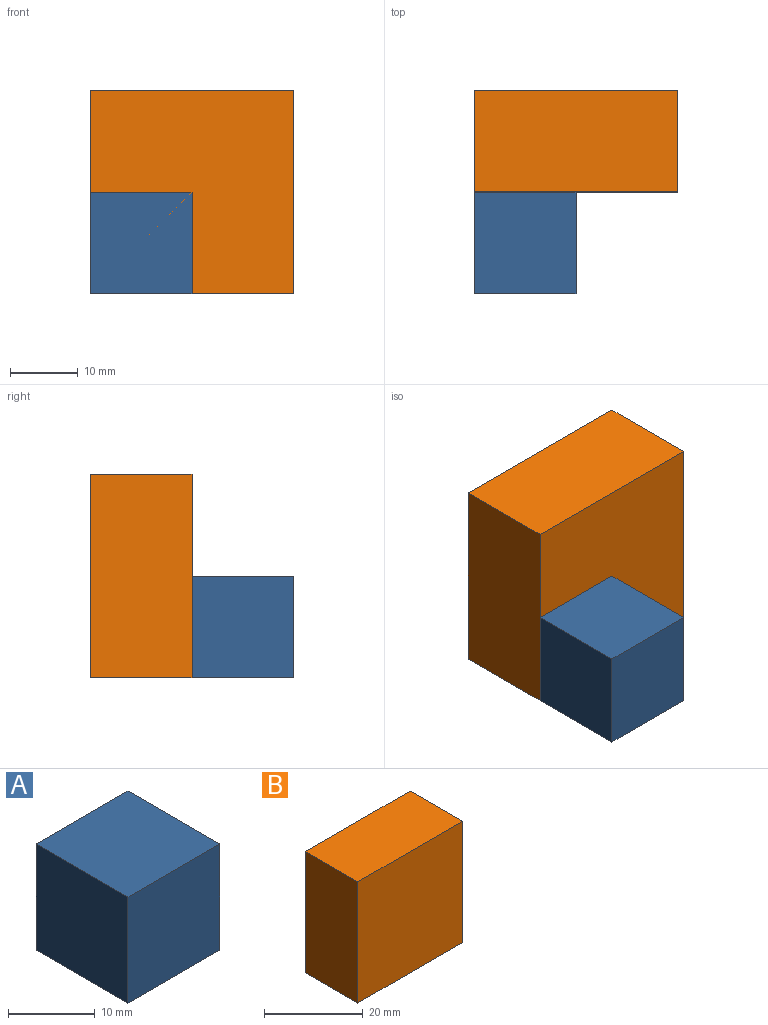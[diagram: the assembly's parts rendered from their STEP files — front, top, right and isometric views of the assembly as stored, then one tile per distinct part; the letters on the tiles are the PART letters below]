
ASSEMBLY  parts=2 mates=1
PART A: 6 faces, bbox 15x15x15 mm
  f0: plane 15x15mm, normal (-1,0,0), area 225mm2, adj f1,f3,f4,f5
  f1: plane 15x15mm, normal (0,0,-1), area 225mm2, adj f0,f2,f4,f5
  f2: plane 15x15mm, normal (1,0,0), area 225mm2, adj f1,f3,f4,f5
  f3: plane 15x15mm, normal (0,0,1), area 225mm2, adj f0,f2,f4,f5
  f4: plane 15x15mm, normal (0,-1,0), area 225mm2, adj f0,f1,f2,f3
  f5: plane 15x15mm, normal (0,1,0), area 225mm2, adj f0,f1,f2,f3
PART B: 6 faces, bbox 30x15x30 mm
  f0: plane 30x15mm, normal (-1,0,0), area 450mm2, adj f1,f3,f4,f5
  f1: plane 30x15mm, normal (0,0,-1), area 450mm2, adj f0,f2,f4,f5
  f2: plane 30x15mm, normal (1,0,0), area 450mm2, adj f1,f3,f4,f5
  f3: plane 30x15mm, normal (0,0,1), area 450mm2, adj f0,f2,f4,f5
  f4: plane 30x30mm, normal (0,-1,0), area 900mm2, adj f0,f1,f2,f3
  f5: plane 30x30mm, normal (0,1,0), area 900mm2, adj f0,f1,f2,f3
PLACE A t=(-1.75,9.17,-1.48)mm
PLACE B t=(-1.75,24.17,-1.48)mm fixed
MATE fastened A.f5 <-> B.f4  axis (0,1,0) through (13.25,9.17,13.52)mm
